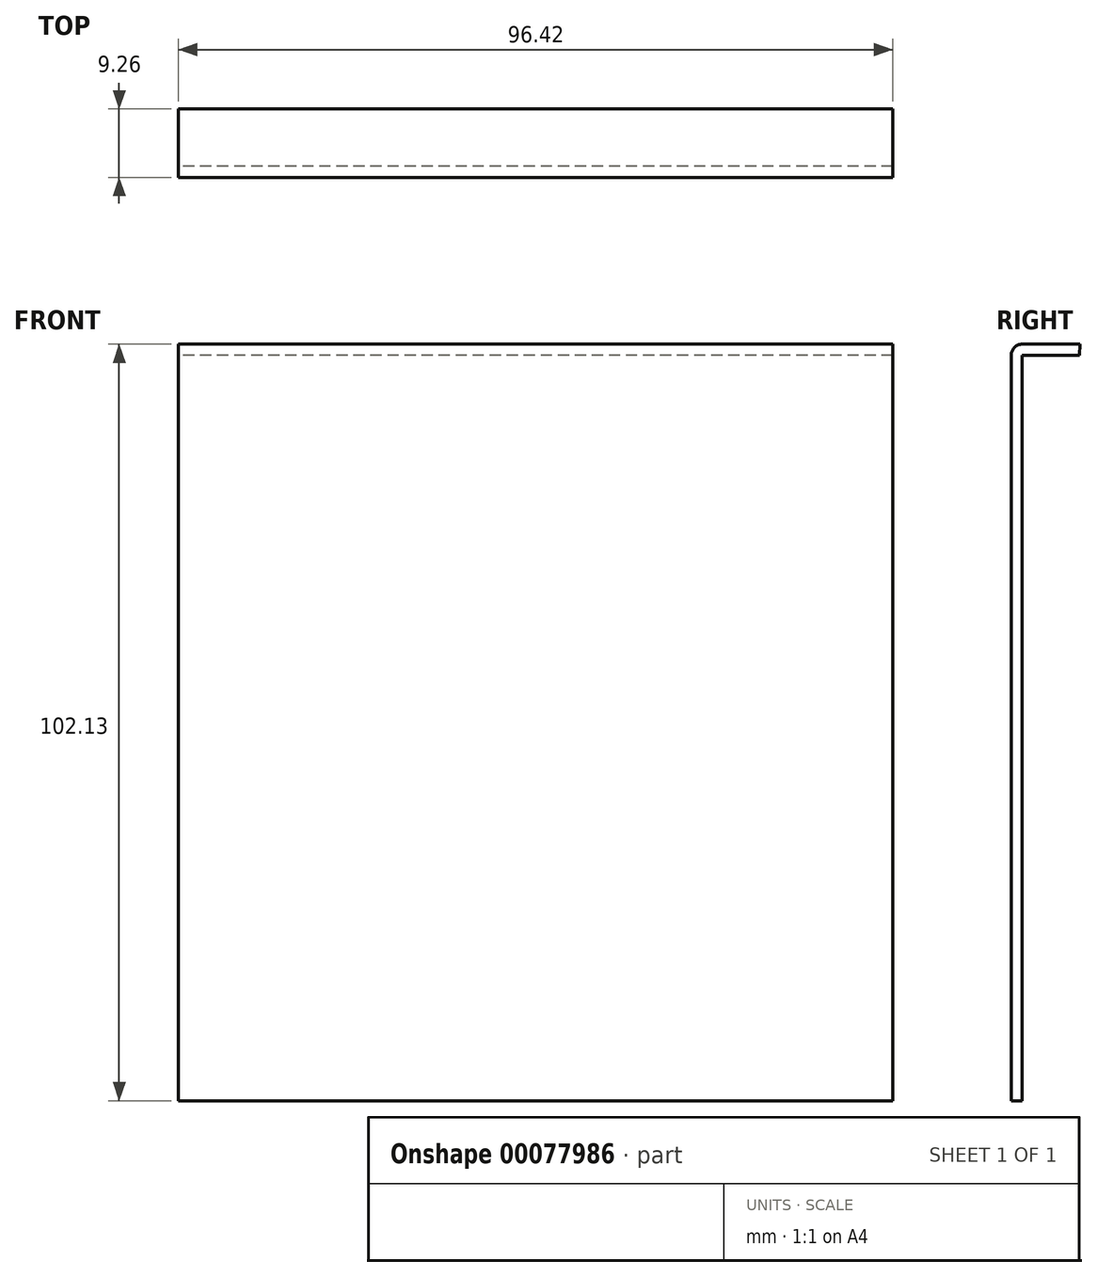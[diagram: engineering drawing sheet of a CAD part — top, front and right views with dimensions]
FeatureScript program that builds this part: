
annotation { "Feature Type Name" : "Feature", "Feature Type Description" : "" }
export const myFeature = defineFeature(function(context is Context, id is Id, definition is map)
    precondition{}
    {
        {
            var Q0;
            Q0=qCreatedBy(makeId("Front.planeOp"),FACE);
            var sketch = newSketch(context, id + "F0", { "sketchPlane" : qUnion([Q0])});
            skLineSegment(sketch, "E0.bottom", {"start": v(48.2, 50.32) * mm, "end": v(-48.2, 50.32) * mm});
            skLineSegment(sketch, "E0.top", {"start": v(48.2, -50.32) * mm, "end": v(-48.2, -50.32) * mm});
            skLineSegment(sketch, "E0.left", {"start": v(48.2, 50.32) * mm, "end": v(48.2, -50.32) * mm});
            skLineSegment(sketch, "E0.right", {"start": v(-48.2, 50.32) * mm, "end": v(-48.2, -50.32) * mm});
            skPoint(sketch, "E0.middle", {"position": v(0, 0) * mm});
            skSolve(sketch);
        }
        {
            var Q0;
            Q0 = qSketchRegion(id + "F0", true);
            extrude(context, id + "F1", {"entities" : qUnion([Q0]), "depth" : 1.5 * mm});
        }
        {
            var Q0;
            Q0=makeQuery(id+"F1.opExtrude","SWEPT_FACE",FACE,{"disambiguationData":[OSD([sQuery(id+"F0.wireOp",EDGE,"E0.left")])]});
            var sketch = newSketch(context, id + "F2", { "sketchPlane" : qUnion([Q0])});
            skArc(sketch, "E1", {"start": v(0, 51.81) * mm, "mid": v(-1.06, 51.38) * mm, "end": v(-1.5, 50.32) * mm});
            skLineSegment(sketch, "E2", {"start": v(0, 51.81) * mm, "end": v(7.76, 51.81) * mm});
            skLineSegment(sketch, "E3", {"start": v(0, 50.32) * mm, "end": v(7.7, 50.32) * mm});
            skLineSegment(sketch, "E4", {"start": v(7.7, 50.32) * mm, "end": v(7.76, 51.81) * mm});
            skLineSegment(sketch, "E5", {"start": v(-1.5, 50.32) * mm, "end": v(0, 50.32) * mm});
            skSolve(sketch);
        }
        {
            var Q0;
            Q0 = qSketchRegion(id + "F2", true);
            var Q1;
            Q1=makeQuery(id+"F1.opExtrude","CAP_VERTEX",VERTEX,{"disambiguationData":[OSD([sQuery(id+"F0.wireOp",EDGE,"E0.bottom"),sQuery(id+"F0.wireOp",EDGE,"E0.right")])],"isStart":false});
            extrude(context, id + "F3", {"entities" : qUnion([Q0]), "operationType" : NewBodyOperationType.ADD, "endBound" : BoundingType.UP_TO_VERTEX, "oppositeDirection" : true, "endBoundEntityVertex" : qUnion([Q1]), "depth" : 25.4 * mm});
        }
    });
